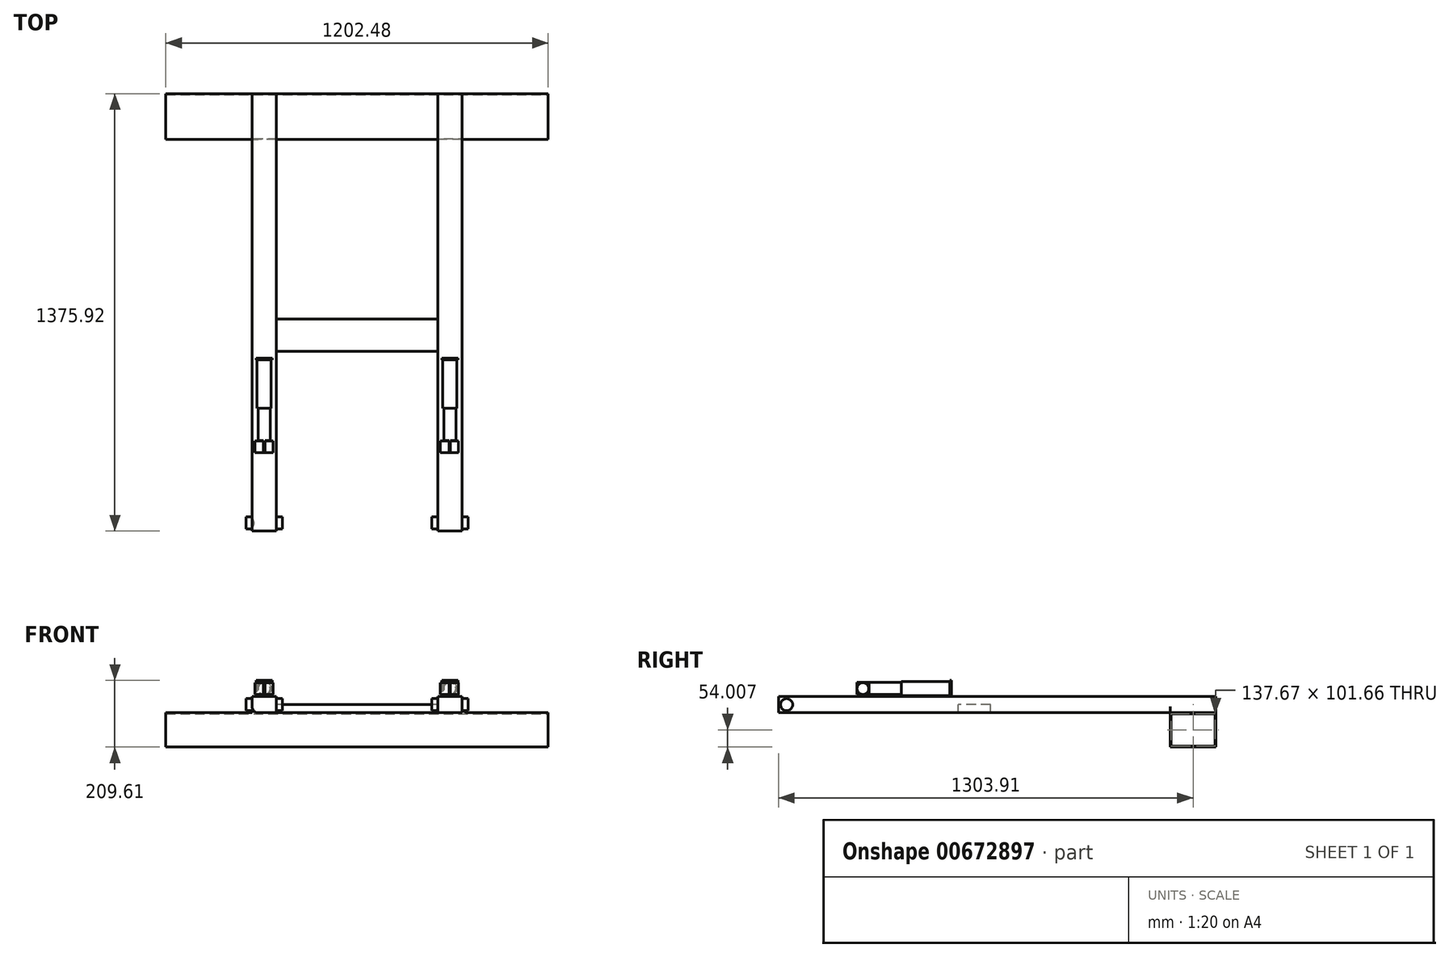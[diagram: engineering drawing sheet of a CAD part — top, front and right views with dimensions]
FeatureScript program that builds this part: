
annotation { "Feature Type Name" : "Feature", "Feature Type Description" : "" }
export const myFeature = defineFeature(function(context is Context, id is Id, definition is map)
    precondition{}
    {
        {
            var Q0;
            Q0=qCreatedBy(makeId("Top.planeOp"),FACE);
            var sketch = newSketch(context, id + "F0", { "sketchPlane" : qUnion([Q0])});
            skLineSegment(sketch, "E0.bottom", {"start": v(601.24, 72) * mm, "end": v(-601.24, 72) * mm});
            skLineSegment(sketch, "E0.top", {"start": v(601.24, -72) * mm, "end": v(-601.24, -72) * mm});
            skLineSegment(sketch, "E0.left", {"start": v(601.24, 72) * mm, "end": v(601.24, -72) * mm});
            skLineSegment(sketch, "E0.right", {"start": v(-601.24, 72) * mm, "end": v(-601.24, -72) * mm});
            skPoint(sketch, "E0.middle", {"position": v(0, 0) * mm});
            skSolve(sketch);
        }
        {
            var Q0;
            Q0=makeQuery(id+"F0.imprint","IMPRINT",FACE,{"disambiguationData":[TD([[makeQuery(id+"F0.imprint","IMPRINT",EDGE,{"derivedFrom":sQuery(id+"F0.wireOp",EDGE,"E0.bottom")}),1.0]])]});
            extrude(context, id + "F1", {"entities" : qUnion([Q0]), "depth" : 108.01 * mm, "offsetDistance" : 25.4 * mm});
        }
        {
            var Q0;
            Q0=makeQuery(id+"F1.opExtrude","SWEPT_FACE",FACE,{"disambiguationData":[OSD([sQuery(id+"F0.wireOp",EDGE,"E0.left")])]});
            var sketch = newSketch(context, id + "F2", { "sketchPlane" : qUnion([Q0])});
            skLineSegment(sketch, "E1.bottom", {"start": v(68.83, 3.18) * mm, "end": v(-68.83, 3.18) * mm});
            skLineSegment(sketch, "E1.top", {"start": v(68.83, 104.84) * mm, "end": v(-68.83, 104.84) * mm});
            skLineSegment(sketch, "E1.left", {"start": v(68.83, 3.18) * mm, "end": v(68.83, 104.84) * mm});
            skLineSegment(sketch, "E1.right", {"start": v(-68.83, 3.18) * mm, "end": v(-68.83, 104.84) * mm});
            skPoint(sketch, "E1.middle", {"position": v(0, 54) * mm});
            skPoint(sketch, "E1.middle.positionSnap0", {"position": v(-72, 54) * mm});
            skPoint(sketch, "E1.centerSnap0", {"position": v(-72, 54) * mm});
            skSolve(sketch);
        }
        {
            var Q0;
            Q0 = qSketchRegion(id + "F2", true);
            extrude(context, id + "F3", {"entities" : qUnion([Q0]), "operationType" : NewBodyOperationType.REMOVE, "oppositeDirection" : true, "depth" : 1202.5 * mm, "offsetDistance" : 25.4 * mm});
        }
        {
            var Q0;
            Q0=makeQuery(id+"F1.opExtrude","CAP_FACE",FACE,{"disambiguationData":[OSD([sQuery(id+"F0.wireOp",EDGE,"E0.bottom"),sQuery(id+"F0.wireOp",EDGE,"E0.top"),sQuery(id+"F0.wireOp",EDGE,"E0.left"),sQuery(id+"F0.wireOp",EDGE,"E0.right")])],"isStart":false});
            var sketch = newSketch(context, id + "F4", { "sketchPlane" : qUnion([Q0])});
            skLineSegment(sketch, "E2", {"start": v(-291.85, 0) * mm, "end": v(291.85, 0) * mm, "construction": true});
            skLineSegment(sketch, "E3", {"start": v(0, 113.31) * mm, "end": v(0, -202.64) * mm, "construction": true});
            skLineSegment(sketch, "E4.bottom", {"start": v(-329.95, 72) * mm, "end": v(-253.75, 72) * mm});
            skLineSegment(sketch, "E4.top", {"start": v(-329.95, -72) * mm, "end": v(-253.75, -72) * mm});
            skLineSegment(sketch, "E4.left", {"start": v(-329.95, 72) * mm, "end": v(-329.95, -72) * mm});
            skLineSegment(sketch, "E4.right", {"start": v(-253.75, 72) * mm, "end": v(-253.75, -72) * mm});
            skPoint(sketch, "E4.middle", {"position": v(-291.85, 0) * mm});
            skLineSegment(sketch, "E5.top", {"start": v(-329.95, -1303.9) * mm, "end": v(-253.75, -1303.9) * mm});
            skLineSegment(sketch, "E5.left", {"start": v(-329.95, -72) * mm, "end": v(-329.95, -1303.9) * mm});
            skLineSegment(sketch, "E5.right", {"start": v(-253.75, -72) * mm, "end": v(-253.75, -1303.9) * mm});
            skLineSegment(sketch, "E6.MirrorCS", {"start": v(329.95, -72) * mm, "end": v(253.75, -72) * mm});
            skLineSegment(sketch, "E7.MirrorCS", {"start": v(329.95, -1303.9) * mm, "end": v(253.75, -1303.9) * mm});
            skLineSegment(sketch, "E8.MirrorCS", {"start": v(329.95, 72) * mm, "end": v(253.75, 72) * mm});
            skLineSegment(sketch, "E9.MirrorCS", {"start": v(253.75, 72) * mm, "end": v(253.75, -72) * mm});
            skLineSegment(sketch, "E10.MirrorCS", {"start": v(329.95, 72) * mm, "end": v(329.95, -72) * mm});
            skLineSegment(sketch, "E11.MirrorCS", {"start": v(253.75, -72) * mm, "end": v(253.75, -1303.9) * mm});
            skLineSegment(sketch, "E12.MirrorCS", {"start": v(329.95, -72) * mm, "end": v(329.95, -1303.9) * mm});
            skPoint(sketch, "E13.MirrorP", {"position": v(291.85, 0) * mm});
            skSolve(sketch);
        }
        {
            var Q0;
            Q0=makeQuery(id+"F4.imprint","IMPRINT",FACE,{"disambiguationData":[TD([[makeQuery(id+"F4.imprint","IMPRINT",EDGE,{"derivedFrom":sQuery(id+"F4.wireOp",EDGE,"E4.bottom")}),1.0]])]});
            var Q1;
            Q1=makeQuery(id+"F4.imprint","IMPRINT",FACE,{"disambiguationData":[TD([[makeQuery(id+"F4.imprint","IMPRINT",EDGE,{"derivedFrom":sQuery(id+"F4.wireOp",EDGE,"E6.MirrorCS")}),-1.0]])]});
            var Q2;
            Q2=makeQuery(id+"F4.imprint","IMPRINT",FACE,{"disambiguationData":[TD([[makeQuery(id+"F4.imprint","IMPRINT",EDGE,{"derivedFrom":sQuery(id+"F4.wireOp",EDGE,"E4.top")}),1.0]])]});
            var Q3;
            Q3=makeQuery(id+"F4.imprint","IMPRINT",FACE,{"disambiguationData":[TD([[makeQuery(id+"F4.imprint","IMPRINT",EDGE,{"derivedFrom":sQuery(id+"F4.wireOp",EDGE,"E6.MirrorCS")}),1.0]])]});
            extrude(context, id + "F5", {"entities" : qUnion([Q0, Q1, Q2, Q3]), "operationType" : NewBodyOperationType.ADD, "depth" : 50.8 * mm, "offsetDistance" : 25.4 * mm});
        }
        {
            var Q0;
            {var subQ0=sQuery(id+"F4.wireOp",EDGE,"E5.right");var subQ1=sQuery(id+"F4.wireOp",EDGE,"E4.right");Q0=makeQuery(id+"F5.boolean.opBoolean","SPLIT",EDGE,{"disambiguationData":[topologyDisambiguationEdgeConnected([makeQuery(id+"F1.opExtrude","CAP_FACE",FACE,{"disambiguationData":[OSD([sQuery(id+"F0.wireOp",EDGE,"E0.bottom"),sQuery(id+"F0.wireOp",EDGE,"E0.top"),sQuery(id+"F0.wireOp",EDGE,"E0.left"),sQuery(id+"F0.wireOp",EDGE,"E0.right")])],"isStart":false})])],"derivedFrom":makeQuery(id+"F5.opExtrude","CAP_EDGE",EDGE,{"disambiguationData":[OSD([subQ1,subQ0])],"isStart":true})});}
            var Q1;
            {var subQ0=sQuery(id+"F4.wireOp",EDGE,"E5.left");var subQ1=sQuery(id+"F4.wireOp",EDGE,"E4.left");Q1=makeQuery(id+"F5.boolean.opBoolean","SPLIT",EDGE,{"disambiguationData":[topologyDisambiguationEdgeConnected([makeQuery(id+"F1.opExtrude","CAP_FACE",FACE,{"disambiguationData":[OSD([sQuery(id+"F0.wireOp",EDGE,"E0.bottom"),sQuery(id+"F0.wireOp",EDGE,"E0.top"),sQuery(id+"F0.wireOp",EDGE,"E0.left"),sQuery(id+"F0.wireOp",EDGE,"E0.right")])],"isStart":false})])],"derivedFrom":makeQuery(id+"F5.opExtrude","CAP_EDGE",EDGE,{"disambiguationData":[OSD([subQ1,subQ0])],"isStart":true})});}
            var Q2;
            {var subQ0=sQuery(id+"F4.wireOp",EDGE,"E11.MirrorCS");var subQ1=sQuery(id+"F4.wireOp",EDGE,"E9.MirrorCS");Q2=makeQuery(id+"F5.boolean.opBoolean","SPLIT",EDGE,{"disambiguationData":[topologyDisambiguationEdgeConnected([makeQuery(id+"F1.opExtrude","CAP_FACE",FACE,{"disambiguationData":[OSD([sQuery(id+"F0.wireOp",EDGE,"E0.bottom"),sQuery(id+"F0.wireOp",EDGE,"E0.top"),sQuery(id+"F0.wireOp",EDGE,"E0.left"),sQuery(id+"F0.wireOp",EDGE,"E0.right")])],"isStart":false})])],"derivedFrom":makeQuery(id+"F5.opExtrude","CAP_EDGE",EDGE,{"disambiguationData":[OSD([subQ1,subQ0])],"isStart":true})});}
            var Q3;
            {var subQ0=sQuery(id+"F4.wireOp",EDGE,"E12.MirrorCS");var subQ1=sQuery(id+"F4.wireOp",EDGE,"E10.MirrorCS");Q3=makeQuery(id+"F5.boolean.opBoolean","SPLIT",EDGE,{"disambiguationData":[topologyDisambiguationEdgeConnected([makeQuery(id+"F1.opExtrude","CAP_FACE",FACE,{"disambiguationData":[OSD([sQuery(id+"F0.wireOp",EDGE,"E0.bottom"),sQuery(id+"F0.wireOp",EDGE,"E0.top"),sQuery(id+"F0.wireOp",EDGE,"E0.left"),sQuery(id+"F0.wireOp",EDGE,"E0.right")])],"isStart":false})])],"derivedFrom":makeQuery(id+"F5.opExtrude","CAP_EDGE",EDGE,{"disambiguationData":[OSD([subQ1,subQ0])],"isStart":true})});}
            fillet(context, id + "F6", {"entities" : qUnion([Q0, Q1, Q2, Q3]), "radius" : 19.05 * mm, "tangentPropagation" : true, "allowEdgeOverflow" : false});
        }
        {
            var Q0;
            Q0=makeQuery(id+"F5.opExtrude","SWEPT_FACE",FACE,{"disambiguationData":[OSD([sQuery(id+"F4.wireOp",EDGE,"E4.right"),sQuery(id+"F4.wireOp",EDGE,"E5.right")])]});
            var sketch = newSketch(context, id + "F7", { "sketchPlane" : qUnion([Q0])});
            skLineSegment(sketch, "E14.bottom", {"start": v(-637.16, 108.01) * mm, "end": v(-738.76, 108.01) * mm});
            skLineSegment(sketch, "E14.top", {"start": v(-637.16, 133.41) * mm, "end": v(-738.76, 133.41) * mm});
            skLineSegment(sketch, "E14.left", {"start": v(-637.16, 108.01) * mm, "end": v(-637.16, 133.41) * mm});
            skLineSegment(sketch, "E14.right", {"start": v(-738.76, 108.01) * mm, "end": v(-738.76, 133.41) * mm});
            skPoint(sketch, "E14.middle", {"position": v(-687.96, 120.71) * mm});
            skPoint(sketch, "E14.middle.positionSnap0", {"position": v(-687.96, 108.01) * mm});
            skPoint(sketch, "E14.middle.positionSnap1", {"position": v(-1303.9, 133.41) * mm});
            skPoint(sketch, "E14.centerSnap0", {"position": v(-687.96, 108.01) * mm});
            skPoint(sketch, "E14.centerSnap1", {"position": v(-1303.9, 133.41) * mm});
            skSolve(sketch);
        }
        {
            var Q0;
            Q0=makeQuery(id+"F7.imprint","IMPRINT",FACE,{"disambiguationData":[TD([[makeQuery(id+"F7.imprint","IMPRINT",EDGE,{"derivedFrom":sQuery(id+"F7.wireOp",EDGE,"E14.bottom")}),-1.0]])]});
            extrude(context, id + "F8", {"entities" : qUnion([Q0]), "operationType" : NewBodyOperationType.ADD, "depth" : 508 * mm, "offsetDistance" : 25.4 * mm});
        }
        {
            var Q0;
            Q0=makeQuery(id+"F5.opExtrude","SWEPT_FACE",FACE,{"disambiguationData":[OSD([sQuery(id+"F4.wireOp",EDGE,"E4.right"),sQuery(id+"F4.wireOp",EDGE,"E5.right")])]});
            var sketch = newSketch(context, id + "F9", { "sketchPlane" : qUnion([Q0])});
            skCircle(sketch, "E15", {"center": v(-1278.5, 133.41) * mm, "radius": 19.05 * mm});
            skPoint(sketch, "E15.centerSnap0", {"position": v(-1303.9, 133.41) * mm});
            skSolve(sketch);
        }
        {
            var Q0;
            Q0 = qSketchRegion(id + "F9", true);
            extrude(context, id + "F10", {"entities" : qUnion([Q0]), "operationType" : NewBodyOperationType.ADD, "depth" : 19.05 * mm, "offsetDistance" : 25.4 * mm});
        }
        {
            var Q0;
            Q0=makeQuery(id+"F9.imprint","IMPRINT",FACE,{"disambiguationData":[TD([[makeQuery(id+"F9.imprint","IMPRINT",EDGE,{"derivedFrom":sQuery(id+"F9.wireOp",EDGE,"E15")}),1.0]])]});
            extrude(context, id + "F11", {"entities" : qUnion([Q0]), "operationType" : NewBodyOperationType.ADD, "oppositeDirection" : true, "depth" : 95.25 * mm, "offsetDistance" : 25.4 * mm});
        }
        {
            var Q0;
            Q0=makeQuery(id+"F5.opExtrude","SWEPT_FACE",FACE,{"disambiguationData":[OSD([sQuery(id+"F4.wireOp",EDGE,"E9.MirrorCS"),sQuery(id+"F4.wireOp",EDGE,"E11.MirrorCS")])]});
            var sketch = newSketch(context, id + "F12", { "sketchPlane" : qUnion([Q0])});
            skCircle(sketch, "E16", {"center": v(1278.5, 133.41) * mm, "radius": 19.05 * mm});
            skPoint(sketch, "E16.centerSnap0", {"position": v(1303.9, 133.41) * mm});
            skSolve(sketch);
        }
        {
            var Q0;
            Q0=makeQuery(id+"F12.imprint","IMPRINT",FACE,{"disambiguationData":[TD([[makeQuery(id+"F12.imprint","IMPRINT",EDGE,{"derivedFrom":sQuery(id+"F12.wireOp",EDGE,"E16")}),1.0]])]});
            extrude(context, id + "F13", {"entities" : qUnion([Q0]), "operationType" : NewBodyOperationType.ADD, "depth" : 19.05 * mm, "offsetDistance" : 25.4 * mm});
        }
        {
            var Q0;
            Q0=makeQuery(id+"F12.imprint","IMPRINT",FACE,{"disambiguationData":[TD([[makeQuery(id+"F12.imprint","IMPRINT",EDGE,{"derivedFrom":sQuery(id+"F12.wireOp",EDGE,"E16")}),1.0]])]});
            extrude(context, id + "F14", {"entities" : qUnion([Q0]), "operationType" : NewBodyOperationType.ADD, "oppositeDirection" : true, "depth" : 95.25 * mm, "offsetDistance" : 25.4 * mm});
        }
        {
            var Q0;
            Q0=makeQuery(id+"F5.opExtrude","CAP_FACE",FACE,{"disambiguationData":[OSD([sQuery(id+"F4.wireOp",EDGE,"E4.bottom"),sQuery(id+"F4.wireOp",EDGE,"E4.left"),sQuery(id+"F4.wireOp",EDGE,"E4.right"),sQuery(id+"F4.wireOp",EDGE,"E5.top"),sQuery(id+"F4.wireOp",EDGE,"E5.left"),sQuery(id+"F4.wireOp",EDGE,"E5.right")])],"isStart":false});
            var sketch = newSketch(context, id + "F15", { "sketchPlane" : qUnion([Q0])});
            skLineSegment(sketch, "E17.bottom", {"start": v(-317.25, -1019.63) * mm, "end": v(-266.45, -1019.63) * mm});
            skLineSegment(sketch, "E17.top", {"start": v(-317.25, -1024.7) * mm, "end": v(-266.45, -1024.7) * mm});
            skLineSegment(sketch, "E17.left", {"start": v(-317.25, -1019.63) * mm, "end": v(-317.25, -1024.7) * mm});
            skLineSegment(sketch, "E17.right", {"start": v(-266.45, -1019.63) * mm, "end": v(-266.45, -1024.7) * mm});
            skPoint(sketch, "E17.middle", {"position": v(-291.85, -1022.17) * mm});
            skPoint(sketch, "E17.middle.positionSnap0", {"position": v(-291.85, -1303.9) * mm});
            skPoint(sketch, "E17.centerSnap0", {"position": v(-291.85, -1303.9) * mm});
            skLineSegment(sketch, "E18.bottom", {"start": v(-317.25, -760.55) * mm, "end": v(-266.45, -760.55) * mm});
            skLineSegment(sketch, "E18.top", {"start": v(-317.25, -765.63) * mm, "end": v(-266.45, -765.63) * mm});
            skLineSegment(sketch, "E18.left", {"start": v(-317.25, -760.55) * mm, "end": v(-317.25, -765.63) * mm});
            skLineSegment(sketch, "E18.right", {"start": v(-266.45, -760.55) * mm, "end": v(-266.45, -765.63) * mm});
            skPoint(sketch, "E18.middle", {"position": v(-291.85, -763.09) * mm});
            skSolve(sketch);
        }
        {
            var Q0;
            Q0=makeQuery(id+"F15.imprint","IMPRINT",FACE,{"disambiguationData":[TD([[makeQuery(id+"F15.imprint","IMPRINT",EDGE,{"derivedFrom":sQuery(id+"F15.wireOp",EDGE,"E18.bottom")}),-1.0]])]});
            extrude(context, id + "F16", {"entities" : qUnion([Q0]), "depth" : 50.8 * mm, "offsetDistance" : 25.4 * mm});
        }
        {
            var Q0;
            Q0=makeQuery(id+"F16.opExtrude","SWEPT_FACE",FACE,{"disambiguationData":[OSD([sQuery(id+"F15.wireOp",EDGE,"E18.top")])]});
            var sketch = newSketch(context, id + "F17", { "sketchPlane" : qUnion([Q0])});
            skCircle(sketch, "E19", {"center": v(-291.85, 184.21) * mm, "radius": 22.23 * mm});
            skPoint(sketch, "E19.centerSnap0", {"position": v(-317.25, 184.21) * mm});
            skPoint(sketch, "E19.centerSnap1", {"position": v(-291.85, 209.61) * mm});
            skSolve(sketch);
        }
        {
            var Q0;
            Q0 = qSketchRegion(id + "F17", true);
            extrude(context, id + "F18", {"entities" : qUnion([Q0]), "operationType" : NewBodyOperationType.ADD, "depth" : 152.4 * mm, "offsetDistance" : 25.4 * mm});
        }
        {
            var Q0;
            Q0=makeQuery(id+"F18.opExtrude","CAP_FACE",FACE,{"disambiguationData":[OSD([sQuery(id+"F17.wireOp",EDGE,"E19")])],"isStart":false});
            var sketch = newSketch(context, id + "F19", { "sketchPlane" : qUnion([Q0])});
            skCircle(sketch, "E20", {"center": v(-291.85, 184.21) * mm, "radius": 19.05 * mm});
            skSolve(sketch);
        }
        {
            var Q0;
            Q0 = qSketchRegion(id + "F19", true);
            extrude(context, id + "F20", {"entities" : qUnion([Q0]), "operationType" : NewBodyOperationType.ADD, "depth" : 101.6 * mm, "offsetDistance" : 25.4 * mm});
        }
        {
            var Q0;
            Q0=makeQuery(id+"F20.opExtrude","CAP_FACE",FACE,{"disambiguationData":[OSD([sQuery(id+"F19.wireOp",EDGE,"E20")])],"isStart":false});
            var sketch = newSketch(context, id + "F21", { "sketchPlane" : qUnion([Q0])});
            skLineSegment(sketch, "E21.bottom", {"start": v(-289.81, 203.26) * mm, "end": v(-293.88, 203.26) * mm});
            skLineSegment(sketch, "E21.top", {"start": v(-289.81, 165.16) * mm, "end": v(-293.88, 165.16) * mm});
            skLineSegment(sketch, "E21.left", {"start": v(-289.81, 203.26) * mm, "end": v(-289.81, 165.16) * mm});
            skLineSegment(sketch, "E21.right", {"start": v(-293.88, 203.26) * mm, "end": v(-293.88, 165.16) * mm});
            skPoint(sketch, "E21.middle", {"position": v(-291.85, 184.21) * mm});
            skSolve(sketch);
        }
        {
            var Q0;
            {var subQ0=makeQuery(id+"F20.opExtrude","CAP_EDGE",EDGE,{"disambiguationData":[OSD([sQuery(id+"F19.wireOp",EDGE,"E20")])],"isStart":false});var subQ2=sQuery(id+"F21.wireOp",EDGE,"E21.left");var subQ3=makeQuery(id+"F21.imprint","INTERSECT",VERTEX,{"disambiguationData":[OD(0.0)],"derivedFrom":[subQ0,subQ2]});Q0=makeQuery(id+"F21.imprint","IMPRINT",FACE,{"disambiguationData":[TD([[makeQuery(id+"F21.imprint","IMPRINT",EDGE,{"disambiguationData":[TD([[subQ3,-1.0]])],"derivedFrom":subQ2}),-1.0]])]});}
            extrude(context, id + "F22", {"entities" : qUnion([Q0]), "operationType" : NewBodyOperationType.ADD, "depth" : 38.1 * mm, "offsetDistance" : 25.4 * mm});
        }
        {
            var Q0;
            Q0=makeQuery(id+"F22.opExtrude","SWEPT_FACE",FACE,{"disambiguationData":[OSD([sQuery(id+"F21.wireOp",EDGE,"E21.left")])]});
            var sketch = newSketch(context, id + "F23", { "sketchPlane" : qUnion([Q0])});
            skCircle(sketch, "E22", {"center": v(-1038.68, 184.21) * mm, "radius": 18.41 * mm});
            skPoint(sketch, "E22.centerSnap0", {"position": v(-1038.68, 203.15) * mm});
            skPoint(sketch, "E22.centerSnap1", {"position": v(-1057.73, 184.21) * mm});
            skSolve(sketch);
        }
        {
            var Q0;
            Q0 = qSketchRegion(id + "F23", true);
            extrude(context, id + "F24", {"entities" : qUnion([Q0]), "operationType" : NewBodyOperationType.ADD, "depth" : 25.4 * mm, "offsetDistance" : 25.4 * mm});
        }
        {
            var Q0;
            Q0=makeQuery(id+"F23.imprint","IMPRINT",FACE,{"disambiguationData":[TD([[makeQuery(id+"F23.imprint","IMPRINT",EDGE,{"derivedFrom":sQuery(id+"F23.wireOp",EDGE,"E22")}),1.0]])]});
            extrude(context, id + "F25", {"entities" : qUnion([Q0]), "operationType" : NewBodyOperationType.ADD, "oppositeDirection" : true, "depth" : 31.75 * mm, "offsetDistance" : 25.4 * mm});
        }
        {
            var Q0;
            Q0=makeQuery(id+"F16.opExtrude","SWEPT_BODY",BODY,{"disambiguationData":[OSD([sQuery(id+"F15.wireOp",EDGE,"E18.bottom"),sQuery(id+"F15.wireOp",EDGE,"E18.top"),sQuery(id+"F15.wireOp",EDGE,"E18.left"),sQuery(id+"F15.wireOp",EDGE,"E18.right")])]});
            transform(context, id + "F26", {"entities" : qUnion([Q0]), "transformType" : TransformType.TRANSLATION_3D, "dx" : 583.7 * mm, "dy" : 0 * mm, "dz" : 0 * mm, "makeCopy" : true});
        }
    });
